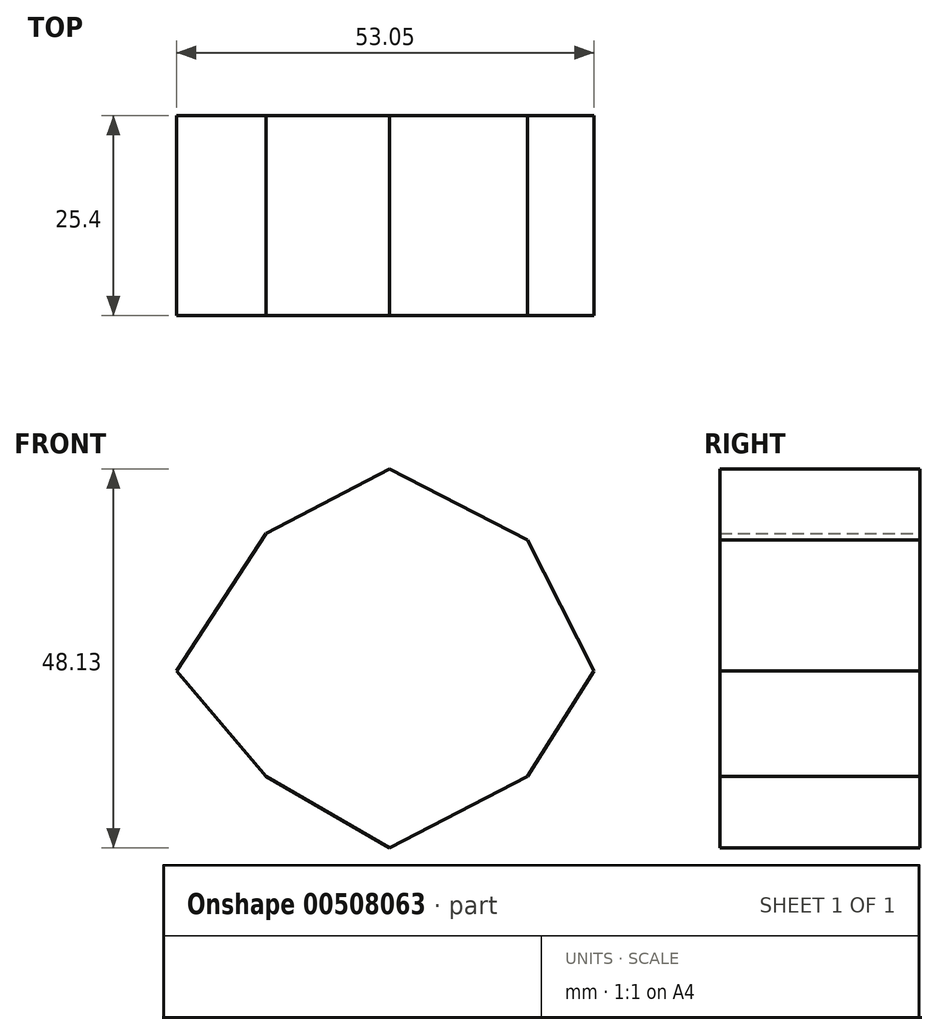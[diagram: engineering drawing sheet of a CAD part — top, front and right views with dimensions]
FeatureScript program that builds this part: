
annotation { "Feature Type Name" : "Feature", "Feature Type Description" : "" }
export const myFeature = defineFeature(function(context is Context, id is Id, definition is map)
    precondition{}
    {
        {
            var Q0;
            Q0=qCreatedBy(makeId("Front.planeOp"),FACE);
            var sketch = newSketch(context, id + "F0", { "sketchPlane" : qUnion([Q0])});
            skLineSegment(sketch, "E0", {"start": v(-15.74, 43.28) * mm, "end": v(0, 51.45) * mm});
            skLineSegment(sketch, "E1", {"start": v(0, 51.45) * mm, "end": v(17.49, 42.4) * mm});
            skLineSegment(sketch, "E2", {"start": v(17.49, 42.4) * mm, "end": v(25.94, 25.8) * mm});
            skLineSegment(sketch, "E3", {"start": v(25.94, 25.8) * mm, "end": v(17.49, 12.39) * mm});
            skLineSegment(sketch, "E4", {"start": v(17.49, 12.39) * mm, "end": v(0, 3.32) * mm});
            skLineSegment(sketch, "E5", {"start": v(0, 3.32) * mm, "end": v(-15.74, 12.39) * mm});
            skLineSegment(sketch, "E6", {"start": v(-15.74, 12.39) * mm, "end": v(-27.1, 25.8) * mm});
            skLineSegment(sketch, "E7", {"start": v(-15.74, 43.28) * mm, "end": v(-27.1, 25.8) * mm});
            skSolve(sketch);
        }
        {
            var Q0;
            Q0 = qSketchRegion(id + "F0", true);
            extrude(context, id + "F1", {"entities" : qUnion([Q0]), "endBound" : BoundingType.SYMMETRIC, "depth" : 25.4 * mm});
        }
    });
